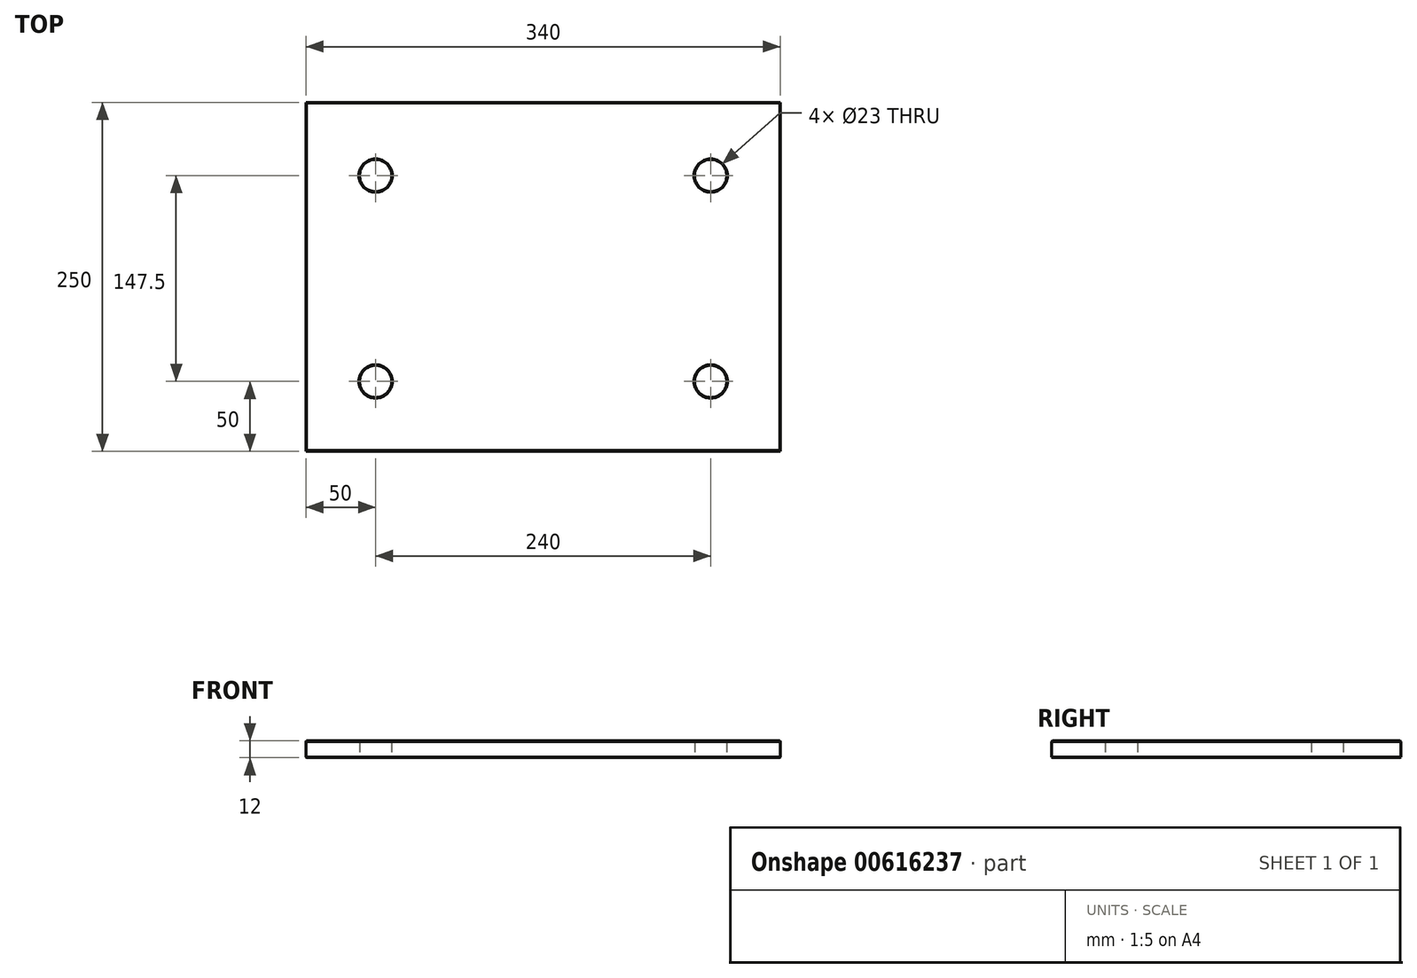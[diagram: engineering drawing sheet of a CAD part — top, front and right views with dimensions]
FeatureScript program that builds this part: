
annotation { "Feature Type Name" : "Feature", "Feature Type Description" : "" }
export const myFeature = defineFeature(function(context is Context, id is Id, definition is map)
    precondition{}
    {
        {
            var Q0;
            Q0=qCreatedBy(makeId("Top.planeOp"),FACE);
            var sketch = newSketch(context, id + "F0", { "sketchPlane" : qUnion([Q0])});
            skLineSegment(sketch, "E0.bottom", {"start": v(170, 125) * mm, "end": v(-170, 125) * mm});
            skLineSegment(sketch, "E0.top", {"start": v(170, -125) * mm, "end": v(-170, -125) * mm});
            skLineSegment(sketch, "E0.left", {"start": v(170, 125) * mm, "end": v(170, -125) * mm});
            skLineSegment(sketch, "E0.right", {"start": v(-170, 125) * mm, "end": v(-170, -125) * mm});
            skPoint(sketch, "E0.middle", {"position": v(0, 0) * mm});
            skLineSegment(sketch, "E1", {"start": v(0, 153.75) * mm, "end": v(0, -169.89) * mm, "construction": true});
            skPoint(sketch, "E1.startSnap0", {"position": v(0, -125) * mm});
            skLineSegment(sketch, "E2", {"start": v(-244.5, 0) * mm, "end": v(239.65, 0) * mm, "construction": true});
            skPoint(sketch, "E2.endSnap0", {"position": v(170, 0) * mm});
            skPoint(sketch, "E3", {"position": v(-120, 72.5) * mm});
            skPoint(sketch, "E4", {"position": v(-120, -75) * mm});
            skLineSegment(sketch, "E5", {"start": v(-120, -167.72) * mm, "end": v(-120, 144.85) * mm, "construction": true});
            skPoint(sketch, "E6.MirrorP", {"position": v(120, 72.5) * mm});
            skPoint(sketch, "E7.MirrorP", {"position": v(120, -75) * mm});
            skSolve(sketch);
        }
        {
            var Q0;
            Q0=makeQuery(id+"F0.imprint","IMPRINT",FACE,{"disambiguationData":[TD([[makeQuery(id+"F0.imprint","IMPRINT",EDGE,{"derivedFrom":sQuery(id+"F0.wireOp",EDGE,"E0.bottom")}),1.0]])]});
            extrude(context, id + "F1", {"entities" : qUnion([Q0]), "depth" : 12 * mm, "offsetDistance" : 25 * mm});
        }
        {
            var Q0;
            Q0=sQuery(id+"F0.wireOp",VERTEX,"E6.MirrorP");
            var Q1;
            Q1=sQuery(id+"F0.wireOp",VERTEX,"E7.MirrorP");
            var Q2;
            Q2=sQuery(id+"F0.wireOp",VERTEX,"E4");
            var Q3;
            Q3=sQuery(id+"F0.wireOp",VERTEX,"E3");
            var Q4;
            Q4=makeQuery(id+"F1.opExtrude","SWEPT_BODY",BODY,{"disambiguationData":[OSD([sQuery(id+"F0.wireOp",EDGE,"E0.bottom"),sQuery(id+"F0.wireOp",EDGE,"E0.top"),sQuery(id+"F0.wireOp",EDGE,"E0.left"),sQuery(id+"F0.wireOp",EDGE,"E0.right")])]});
            hole(context, id + "F2", {"style" : HoleStyle.SIMPLE, "endStyle" : HoleEndStyle.THROUGH, "oppositeDirection" : true, "holeDiameter" : 23 * mm, "majorDiameter" : 5 * mm, "isTappedThrough" : true, "tappedDepth" : 12 * mm, "tapClearance" : 3, "locations" : qUnion([Q0, Q1, Q2, Q3]), "scope" : qUnion([Q4])});
        }
        {
            var Q0;
            Q0=makeQuery(id+"F1.opExtrude","CAP_FACE",FACE,{"disambiguationData":[OSD([sQuery(id+"F0.wireOp",EDGE,"E0.bottom"),sQuery(id+"F0.wireOp",EDGE,"E0.top"),sQuery(id+"F0.wireOp",EDGE,"E0.left"),sQuery(id+"F0.wireOp",EDGE,"E0.right")])],"isStart":false});
            var Q1;
            Q1=makeQuery(id+"F1.opExtrude","CAP_FACE",FACE,{"disambiguationData":[OSD([sQuery(id+"F0.wireOp",EDGE,"E0.bottom"),sQuery(id+"F0.wireOp",EDGE,"E0.top"),sQuery(id+"F0.wireOp",EDGE,"E0.left"),sQuery(id+"F0.wireOp",EDGE,"E0.right")])],"isStart":true});
            chamfer(context, id + "F3", {"entities" : qUnion([Q0, Q1]), "width" : .5 * mm, "tangentPropagation" : true});
        }
    });
